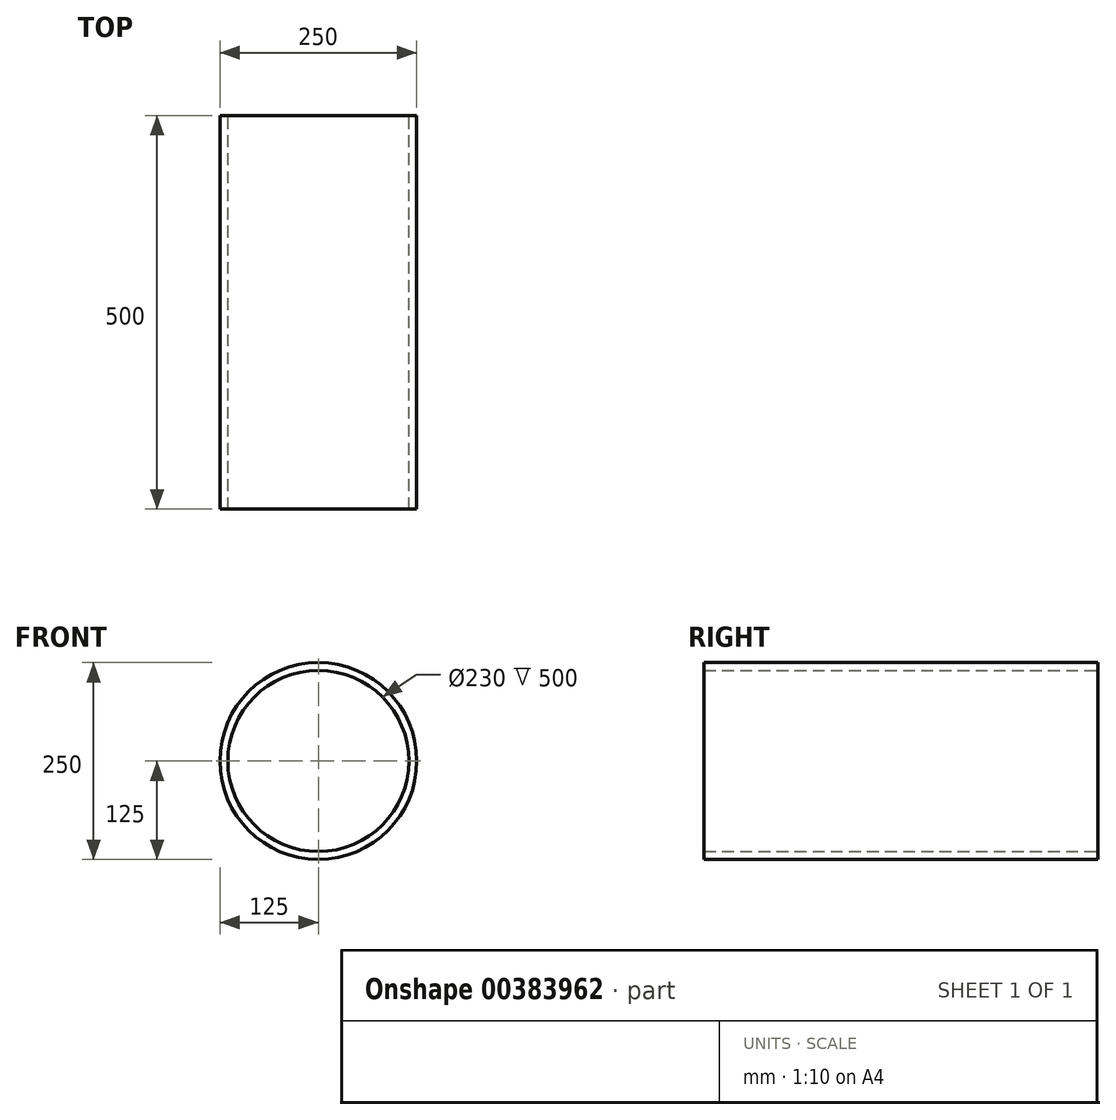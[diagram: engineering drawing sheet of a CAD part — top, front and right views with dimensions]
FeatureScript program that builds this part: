
annotation { "Feature Type Name" : "Feature", "Feature Type Description" : "" }
export const myFeature = defineFeature(function(context is Context, id is Id, definition is map)
    precondition{}
    {
        {
            var Q0;
            Q0=qCreatedBy(makeId("Front.planeOp"),FACE);
            var sketch = newSketch(context, id + "F0", { "sketchPlane" : qUnion([Q0])});
            skCircle(sketch, "E0", {"center": v(0, 0) * mm, "radius": 125 * mm});
            skSolve(sketch);
        }
        {
            var Q0;
            Q0 = qSketchRegion(id + "F0", true);
            extrude(context, id + "F1", {"entities" : qUnion([Q0]), "depth" : 500 * mm});
        }
        {
            var Q0;
            Q0=makeQuery(id+"F1.opExtrude","CAP_FACE",FACE,{"disambiguationData":[OSD([sQuery(id+"F0.wireOp",EDGE,"E0")])],"isStart":false});
            var Q1;
            Q1=makeQuery(id+"F1.opExtrude","CAP_FACE",FACE,{"disambiguationData":[OSD([sQuery(id+"F0.wireOp",EDGE,"E0")])],"isStart":true});
            var Q2;
            Q2=makeQuery(id+"F1.opExtrude","SWEPT_BODY",BODY,{"disambiguationData":[OSD([sQuery(id+"FF9Xk7hbtk2z74Y_0.wireOp",EDGE,"4NDKS2yC-K3nY-Xg0L-782P-uufcIwUOuggp")])]});
            shell(context, id + "F2", {"entities" : qUnion([Q0, Q1]), "parts" : qUnion([Q2]), "thickness" : 10 * mm});
        }
        {
            var Q0;
            Q0=qCreatedBy(makeId("Front.planeOp"),FACE);
            var sketch = newSketch(context, id + "F3", { "sketchPlane" : qUnion([Q0])});
            skCircle(sketch, "E1", {"center": v(0, 0) * mm, "radius": 115 * mm});
            skSolve(sketch);
        }
        {
            var Q0;
            Q0 = qSketchRegion(id + "F3", true);
            extrude(context, id + "F4", {"entities" : qUnion([Q0]), "depth" : 500 * mm});
        }
    });
